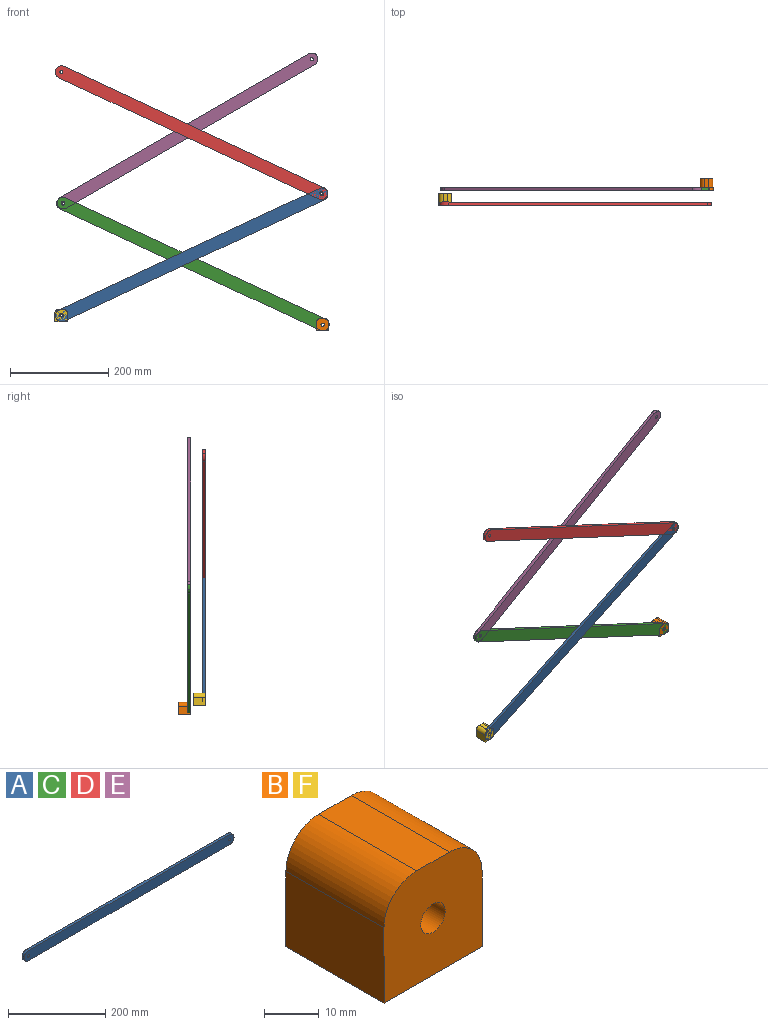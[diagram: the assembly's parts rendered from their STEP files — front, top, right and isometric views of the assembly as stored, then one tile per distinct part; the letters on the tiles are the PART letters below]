
ASSEMBLY  parts=6 mates=4
PART A: 10 faces, bbox 609.6x6.4x25.4 mm
  f0: plane 583.85x6.35mm, normal (0,0,1), area 3707.4mm2, adj f2,f3,f5,f6
  f1: plane 583.85x6.35mm, normal (0,0,-1), area 3707.4mm2, adj f2,f3,f4,f7
  f2: plane 609.6x25.4mm, normal (0,-1,0), area 15278.2mm2, adj f0,f1,f4,f5,f6,f7,f8,f9
  f3: plane 609.6x25.4mm, normal (0,1,0), area 15278.2mm2, adj f0,f1,f4,f5,f6,f7,f8,f9
  f4: cylinder r=12.88mm len=12.88mm, axis (0,1,0), area 127.3mm2, adj f1,f2,f3,f5
  f5: cylinder r=12.88mm len=12.88mm, axis (0,-1,0), area 127.3mm2, adj f0,f2,f3,f4
  f6: cylinder r=12.88mm len=12.88mm, axis (0,1,0), area 127.3mm2, adj f0,f2,f3,f7
  f7: cylinder r=12.88mm len=12.88mm, axis (0,-1,0), area 127.3mm2, adj f1,f2,f3,f6
  f8: cylinder r=3.17mm len=6.35mm, axis (0,1,0), area 126.7mm2, adj f2,f3
  f9: cylinder r=3.17mm len=6.35mm, axis (0,1,0), area 126.7mm2, adj f2,f3
PART B: 9 faces, bbox 25.4x25.4x25.4 mm
  f0: plane 25.4x25.4mm, normal (0,0,-1), area 645.2mm2, adj f1,f5,f6,f7
  f1: plane 25.4x16.92mm, normal (1,0,0), area 429.8mm2, adj f0,f2,f6,f7
  f2: cylinder r=8.48mm len=25.4mm, axis (0,1,0), area 338.3mm2, adj f1,f3,f6,f7
  f3: plane 25.4x8.44mm, normal (0,0,1), area 214.4mm2, adj f2,f4,f6,f7
  f4: cylinder r=8.48mm len=25.4mm, axis (0,1,0), area 338.3mm2, adj f3,f5,f6,f7
  f5: plane 25.4x16.92mm, normal (-1,0,0), area 429.8mm2, adj f0,f4,f6,f7
  f6: plane 25.4x25.4mm, normal (0,-1,0), area 582.6mm2, adj f0,f1,f2,f3,f4,f5,f8
  f7: plane 25.4x25.4mm, normal (0,1,0), area 582.6mm2, adj f0,f1,f2,f3,f4,f5,f8
  f8: cylinder r=3.17mm len=25.4mm, axis (0,1,0), area 506.7mm2, adj f6,f7
PART C: same geometry as A
PART D: same geometry as A
PART E: same geometry as A
PART F: same geometry as B
PLACE A rot(axis=(0,-1,0),25deg) t=(71.72,-9.53,-213.1)mm
PLACE B t=(511.14,39.34,-284.19)mm
PLACE C rot(axis=(0,1,0),25deg) t=(76.4,20.29,-59.8)mm
PLACE D rot(axis=(0,1,0),25deg) t=(73.31,-9.53,207.81)mm
PLACE E rot(axis=(0,-1,0),30deg) t=(71.07,20.29,23.16)mm
PLACE F t=(-21.19,9.52,-265.41)mm
MATE pin_slot A.f4 <-> F.f8  axis (0,-1,0) through (-7.07,-15.88,-252.71)mm
MATE pin_slot D.f6 <-> A.f6  axis (0,-1,0) through (521.32,-15.88,-4.35)mm
MATE pin_slot E.f4 <-> C.f8  axis (0,-1,0) through (-3.97,13.94,-23.16)mm
MATE pin_slot B.f8 <-> C.f9  axis (0,-1,0) through (523.84,13.94,-271.49)mm
